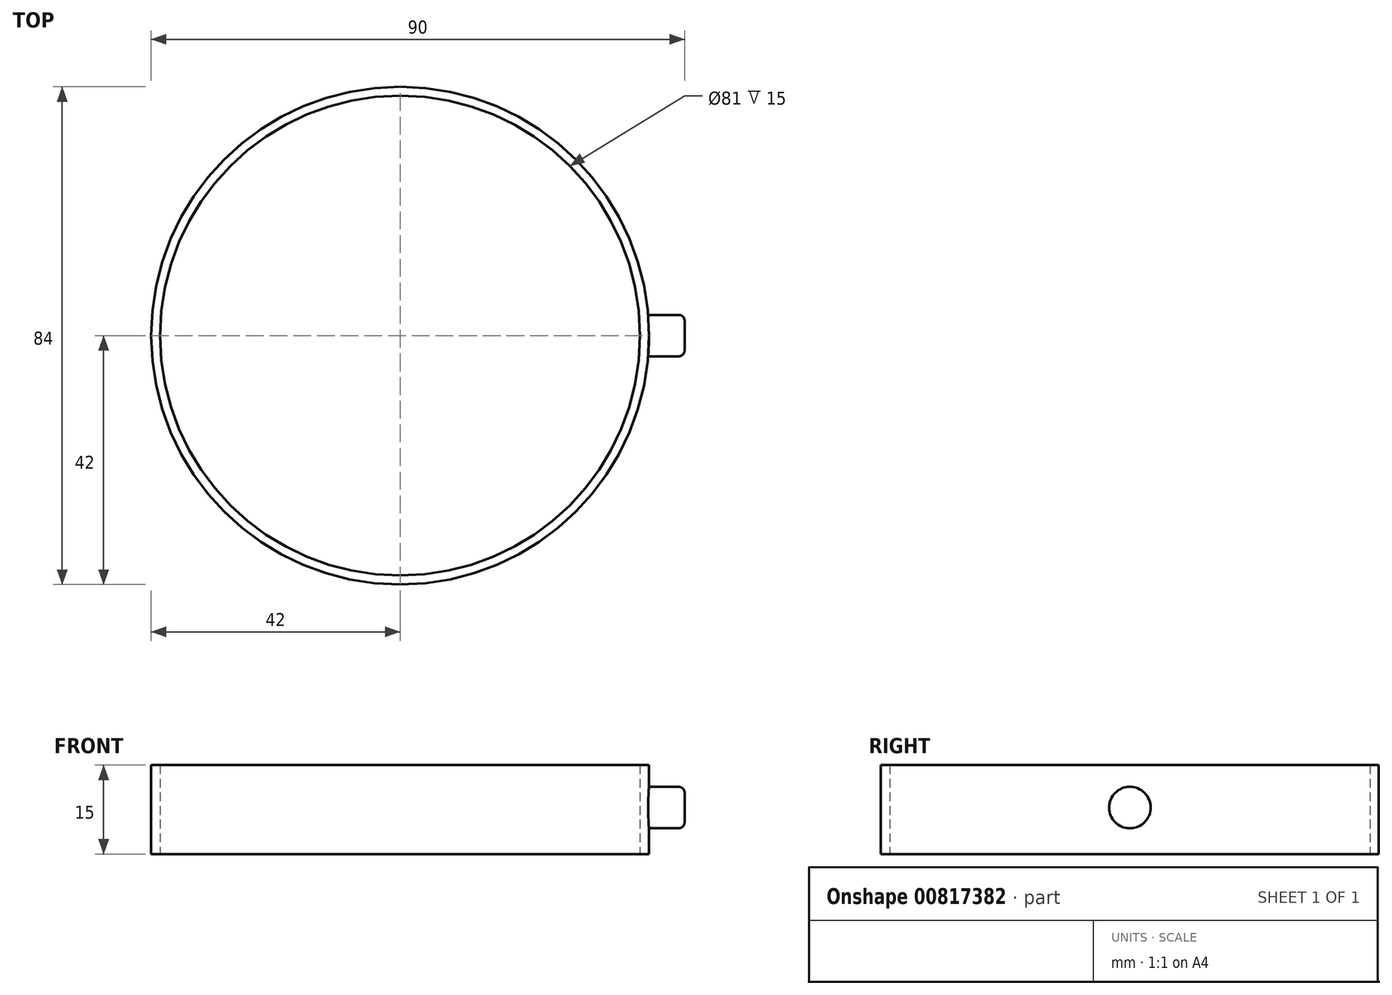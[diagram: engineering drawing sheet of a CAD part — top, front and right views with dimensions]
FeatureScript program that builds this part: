
annotation { "Feature Type Name" : "Feature", "Feature Type Description" : "" }
export const myFeature = defineFeature(function(context is Context, id is Id, definition is map)
    precondition{}
    {
        {
            var Q0;
            Q0=qCreatedBy(makeId("Top.planeOp"),FACE);
            var sketch = newSketch(context, id + "F0", { "sketchPlane" : qUnion([Q0])});
            skCircle(sketch, "E0", {"center": v(0, 0) * mm, "radius": 40.5 * mm});
            skCircle(sketch, "E1.0", {"center": v(0, 0) * mm, "radius": 0.75 * mm});
            skCircle(sketch, "E2.0", {"center": v(0, 0) * mm, "radius": 42 * mm});
            skSolve(sketch);
        }
        {
            var Q0;
            Q0=makeQuery(id+"F0.imprint","IMPRINT",FACE,{"disambiguationData":[TD([[makeQuery(id+"F0.imprint","IMPRINT",EDGE,{"derivedFrom":sQuery(id+"F0.wireOp",EDGE,"E0")}),-1.0]])]});
            extrude(context, id + "F1", {"entities" : qUnion([Q0]), "depth" : 15 * mm, "offsetDistance" : 25 * mm});
        }
        {
            var Q0;
            Q0=qCreatedBy(makeId("Right.planeOp"),FACE);
            cPlane(context, id + "F2", {"entities" : qUnion([Q0]), "cplaneType" : CPlaneType.OFFSET, "offset" : 41 * mm, "width" : 150 * mm, "height" : 150 * mm});
        }
        {
            var Q0;
            Q0=qCreatedBy(id+"F2.planeOp",FACE);
            var sketch = newSketch(context, id + "F3", { "sketchPlane" : qUnion([Q0])});
            skCircle(sketch, "E3", {"center": v(0, 7.84) * mm, "radius": 3.5 * mm});
            skSolve(sketch);
        }
        {
            var Q0;
            Q0 = qSketchRegion(id + "F3", true);
            extrude(context, id + "F4", {"entities" : qUnion([Q0]), "operationType" : NewBodyOperationType.ADD, "depth" : 7 * mm, "offsetDistance" : 25 * mm});
        }
        {
            var Q0;
            Q0=makeQuery(id+"F4.opExtrude","CAP_EDGE",EDGE,{"disambiguationData":[OSD([sQuery(id+"F3.wireOp",EDGE,"E3")])],"isStart":false});
            fillet(context, id + "F5", {"entities" : qUnion([Q0]), "radius" : 1 * mm, "tangentPropagation" : true, "allowEdgeOverflow" : false});
        }
    });
